# Revit family: Washing_Machine-Floor_Drain-KOHLER-K-45966T_1
name_source: partatom
category: Plumbing Fixtures
units: mm (PartAtom-declared; Revit-internal decimal feet)

## family parameters
Cut with Voids When Loaded = No
Host = Face
Maintain Annotation Orientation = No
OmniClass Number = 23.39.29.11
OmniClass Title = Waste Water Drains
Part Type = Normal
Room Calculation Point = No
Round Connector Dimension = Use Diameter
Shared = No

## types (2) — shared parameters
ADA Compliant = No
Assembly Code = D2010400
CW Connection = No
Cold Water Inlet = Cold Water Inlet
Date Modified = 02/11/2022
Default Elevation = 0"
Drain Included = Yes
Finish = Kohler-Metal-CP-Polished_Chrome
HW Connection = No
Height = 3 3/8"
Hot Water Inlet = Hot Water Inlet
Length = 3 15/16"
Manufacturer = KOHLER Co.
Master Format 2014 = 22 41 16
Master Format 2014 Name = Residential Lavatories and Sinks
Material = Premium Metal Construction
URL = http://www.kohler.com.cn
Vent Connection = No
Waste Connection = Yes
Waste Water Outlet = Waste Water Outlet
WaterSense Certified = No
Width = 3 15/16"

## per-type parameters (varying)
| type | Description | K-45966T | K-45966T-B | Model | Product Documentation Link | Product Page URL | Type |
| B, CP-Polished Chrome | WASHING MACHINE FLOOR DRAIN | No | Yes | K-45966T-B-CP | https://files.kohler.com.cn | https://www.kohler.com.cn | 1 |
| CP-Polished Chrome | WASHING MACHINE DRAIN | Yes | No | K-45966T-CP |  |  | 2 |

## geometry (parser evidence)
native form markers: Sweep x5
no freeform markers — native parametric forms only
